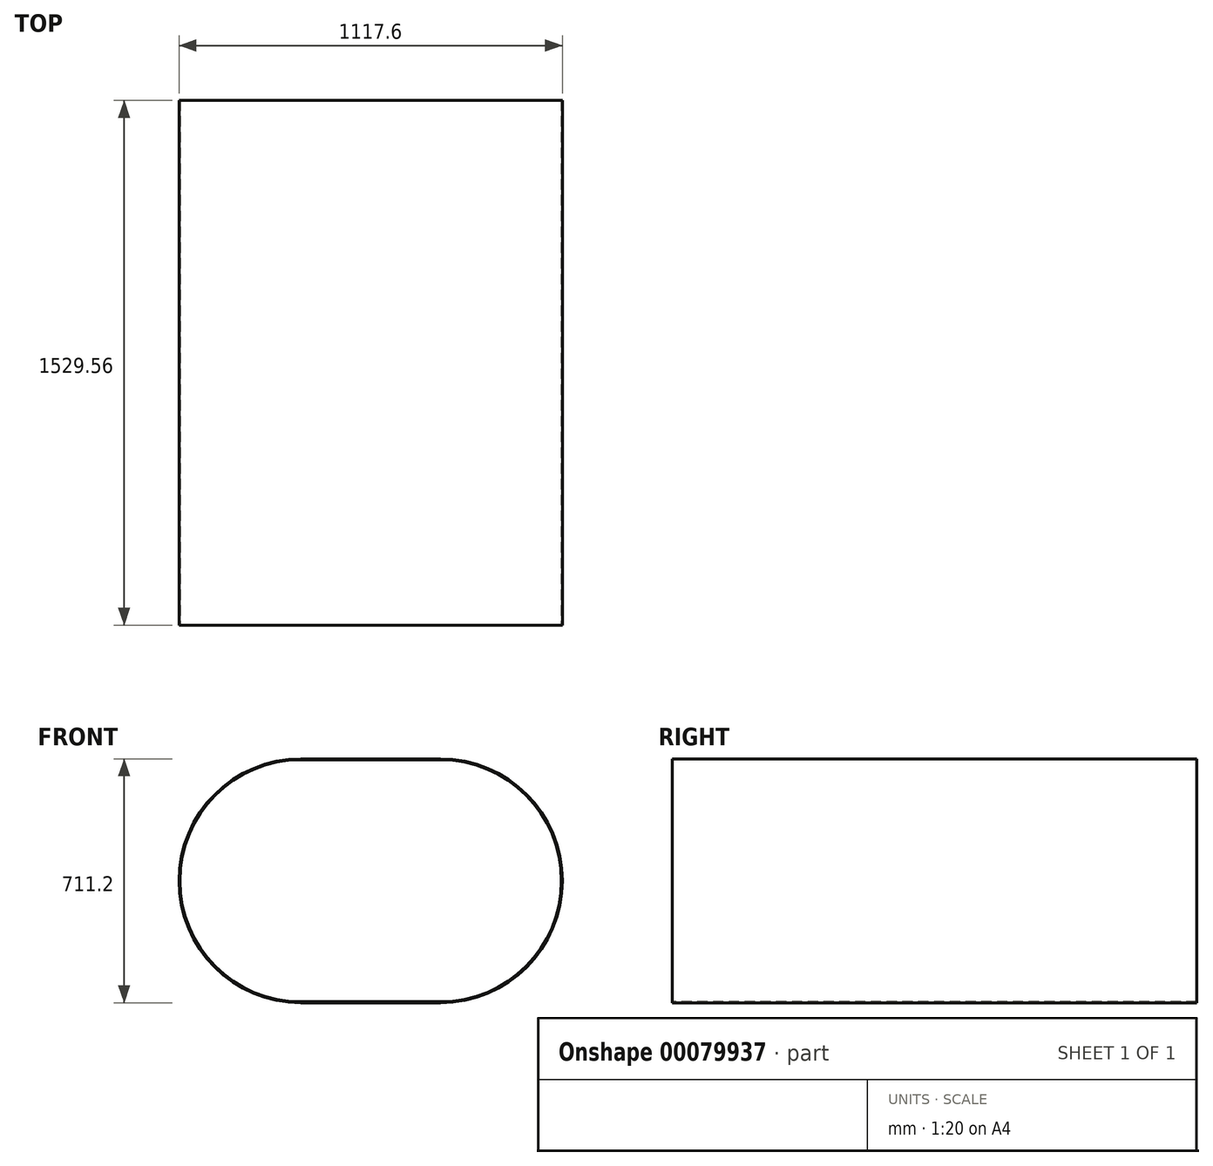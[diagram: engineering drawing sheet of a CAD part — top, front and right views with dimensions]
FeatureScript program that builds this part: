
annotation { "Feature Type Name" : "Feature", "Feature Type Description" : "" }
export const myFeature = defineFeature(function(context is Context, id is Id, definition is map)
    precondition{}
    {
        {
            var Q0;
            Q0=qCreatedBy(makeId("Front.planeOp"),FACE);
            var sketch = newSketch(context, id + "F0", { "sketchPlane" : qUnion([Q0])});
            skArc(sketch, "E0", {"start": v(-203.2, 355.6) * mm, "mid": v(-558.8, 0) * mm, "end": v(-203.2, -355.6) * mm});
            skArc(sketch, "E1", {"start": v(203.2, 355.6) * mm, "mid": v(558.8, 0) * mm, "end": v(203.2, -355.6) * mm});
            skLineSegment(sketch, "E2", {"start": v(-203.2, 355.6) * mm, "end": v(203.2, 355.6) * mm});
            skLineSegment(sketch, "E3", {"start": v(-203.2, -355.6) * mm, "end": v(203.2, -355.6) * mm});
            skLineSegment(sketch, "E4", {"start": v(203.2, 0) * mm, "end": v(-203.2, 0) * mm});
            skPoint(sketch, "E5", {"position": v(-558.8, 0) * mm});
            skPoint(sketch, "E6", {"position": v(558.8, 0) * mm});
            skSolve(sketch);
        }
        {
            var Q0;
            Q0 = qSketchRegion(id + "F0", true);
            extrude(context, id + "F1", {"entities" : qUnion([Q0]), "depth" : 762 * mm});
        }
        {
            var Q0;
            Q0=makeQuery(id+"F1.opExtrude","CAP_FACE",FACE,{"disambiguationData":[OSD([sQuery(id+"F0.wireOp",EDGE,"E0"),sQuery(id+"F0.wireOp",EDGE,"E1"),sQuery(id+"F0.wireOp",EDGE,"E2"),sQuery(id+"F0.wireOp",EDGE,"E3")])],"isStart":false});
            var sketch = newSketch(context, id + "F2", { "sketchPlane" : qUnion([Q0])});
            skLineSegment(sketch, "E7.0", {"start": v(203.2, 352.82) * mm, "end": v(-203.2, 352.82) * mm});
            skArc(sketch, "E7.1", {"start": v(203.2, -352.82) * mm, "mid": v(556.02, 0) * mm, "end": v(203.2, 352.82) * mm});
            skLineSegment(sketch, "E7.2", {"start": v(-203.2, -352.82) * mm, "end": v(203.2, -352.82) * mm});
            skArc(sketch, "E7.3", {"start": v(-203.2, 352.82) * mm, "mid": v(-556.02, 0) * mm, "end": v(-203.2, -352.82) * mm});
            skSolve(sketch);
        }
        {
            var Q0;
            Q0 = qSketchRegion(id + "F2", true);
            extrude(context, id + "F3", {"entities" : qUnion([Q0]), "operationType" : NewBodyOperationType.REMOVE, "endBound" : BoundingType.UP_TO_NEXT, "oppositeDirection" : true, "depth" : 25.4 * mm});
        }
        {
            var Q0;
            Q0=makeQuery(id+"F1.opExtrude","CAP_FACE",FACE,{"disambiguationData":[OSD([sQuery(id+"F0.wireOp",EDGE,"E0"),sQuery(id+"F0.wireOp",EDGE,"E1"),sQuery(id+"F0.wireOp",EDGE,"E2"),sQuery(id+"F0.wireOp",EDGE,"E3")])],"isStart":false});
            var sketch = newSketch(context, id + "F4", { "sketchPlane" : qUnion([Q0])});
            skSolve(sketch);
        }
        {
            var Q0;
            Q0 = qSketchRegion(id + "F4", true);
            var Q1;
            Q1=makeQuery(id+"F4.imprint","IMPRINT",FACE,{"disambiguationData":[TD([[makeQuery(id+"F4.imprint","IMPRINT",EDGE,{"derivedFrom":makeQuery(id+"F1.opExtrude","CAP_EDGE",EDGE,{"disambiguationData":[OSD([sQuery(id+"F0.wireOp",EDGE,"E0")])],"isStart":false})}),1.0]])]});
            var Q2;
            Q2=makeQuery(id+"F4.imprint","IMPRINT",FACE,{"disambiguationData":[TD([[makeQuery(id+"F4.imprint","IMPRINT",EDGE,{"derivedFrom":makeQuery(id+"F3.boolean.opBoolean","COPY",EDGE,{"derivedFrom":makeQuery(id+"F3.opExtrude","CAP_EDGE",EDGE,{"disambiguationData":[OSD([sQuery(id+"F2.wireOp",EDGE,"E7.0")])],"isStart":true})})}),1.0]])]});
            extrude(context, id + "F5", {"entities" : qUnion([Q0, Q1, Q2]), "operationType" : NewBodyOperationType.ADD, "depth" : 2.78 * mm});
        }
        {
            var Q0;
            Q0=makeQuery(id+"F1.opExtrude","SWEPT_BODY",BODY,{"disambiguationData":[OSD([sQuery(id+"F0.wireOp",EDGE,"E0"),sQuery(id+"F0.wireOp",EDGE,"E1"),sQuery(id+"F0.wireOp",EDGE,"E2"),sQuery(id+"F0.wireOp",EDGE,"E3")])]});
            var Q1;
            Q1=qCreatedBy(makeId("Front.planeOp"),FACE);
            mirror(context, id + "F6", {"operationType" : NewBodyOperationType.ADD, "entities" : qUnion([Q0]), "mirrorPlane" : qUnion([Q1])});
        }
    });
